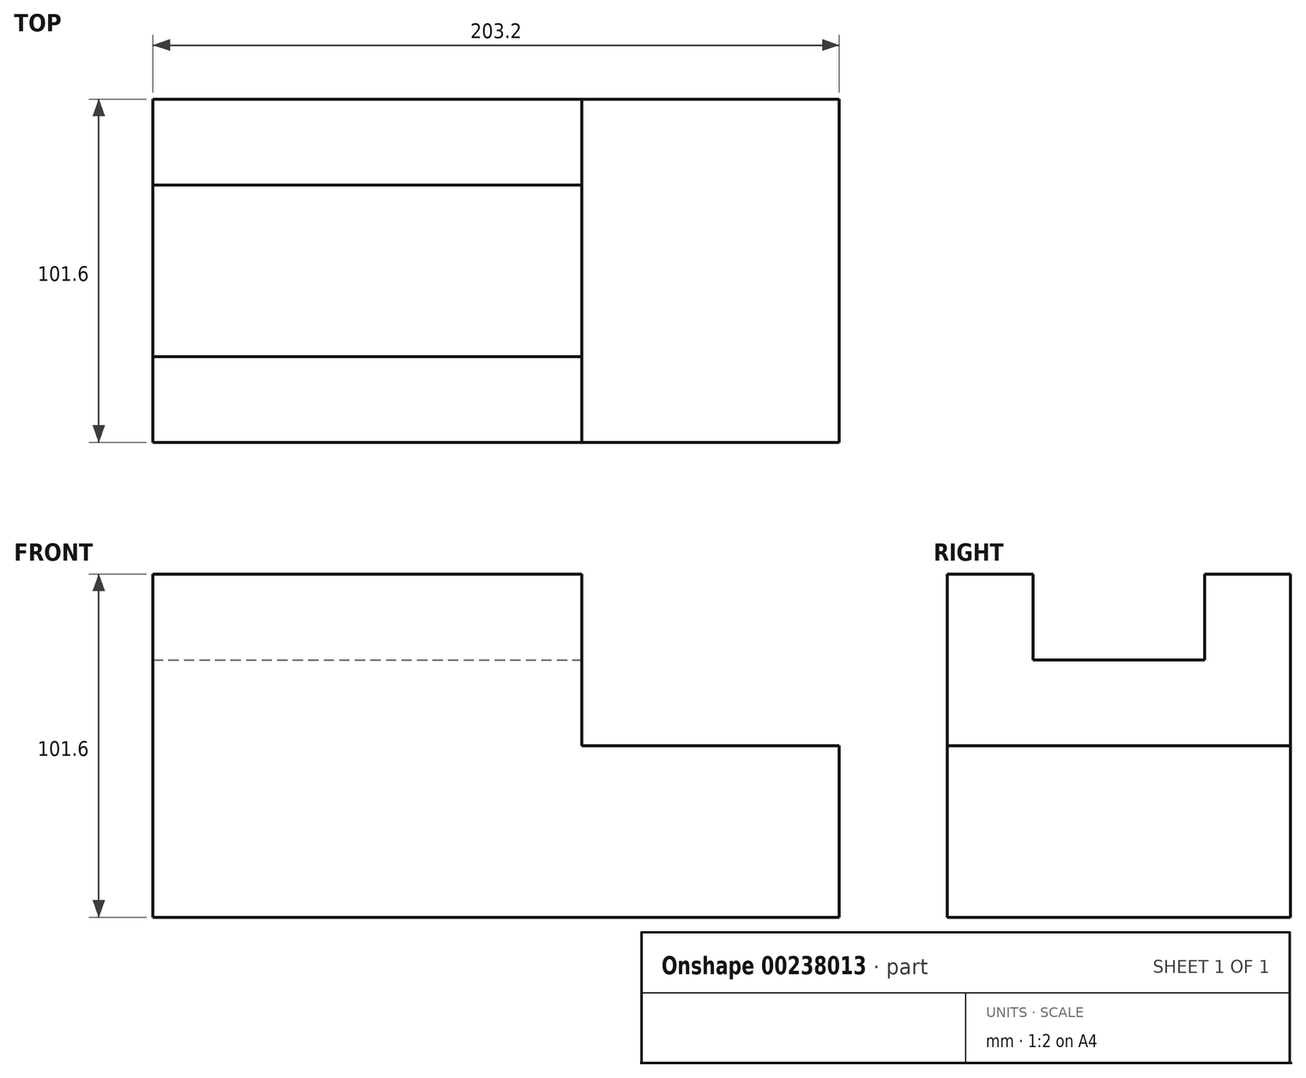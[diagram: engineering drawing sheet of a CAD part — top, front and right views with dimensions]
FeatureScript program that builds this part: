
annotation { "Feature Type Name" : "Feature", "Feature Type Description" : "" }
export const myFeature = defineFeature(function(context is Context, id is Id, definition is map)
    precondition{}
    {
        {
            var Q0;
            Q0=qCreatedBy(makeId("Front.planeOp"),FACE);
            var sketch = newSketch(context, id + "F0", { "sketchPlane" : qUnion([Q0])});
            skLineSegment(sketch, "E0.bottom", {"start": v(-132.5, 56.94) * mm, "end": v(70.7, 56.94) * mm});
            skLineSegment(sketch, "E0.top", {"start": v(-132.5, -44.66) * mm, "end": v(70.7, -44.66) * mm});
            skLineSegment(sketch, "E0.left", {"start": v(-132.5, 56.94) * mm, "end": v(-132.5, -44.66) * mm});
            skLineSegment(sketch, "E0.right", {"start": v(70.7, 56.94) * mm, "end": v(70.7, -44.66) * mm});
            skSolve(sketch);
        }
        {
            var Q0;
            Q0=makeQuery(id+"F0.imprint","IMPRINT",FACE,{"disambiguationData":[TD([[makeQuery(id+"F0.imprint","IMPRINT",EDGE,{"derivedFrom":sQuery(id+"F0.wireOp",EDGE,"E0.bottom")}),-1.0]])]});
            extrude(context, id + "F1", {"entities" : qUnion([Q0]), "depth" : 101.6 * mm});
        }
        {
            var Q0;
            Q0=makeQuery(id+"F1.opExtrude","CAP_FACE",FACE,{"disambiguationData":[OSD([sQuery(id+"F0.wireOp",EDGE,"E0.bottom"),sQuery(id+"F0.wireOp",EDGE,"E0.top"),sQuery(id+"F0.wireOp",EDGE,"E0.left"),sQuery(id+"F0.wireOp",EDGE,"E0.right")])],"isStart":false});
            var sketch = newSketch(context, id + "F2", { "sketchPlane" : qUnion([Q0])});
            skLineSegment(sketch, "E1.bottom", {"start": v(70.7, 56.94) * mm, "end": v(-5.5, 56.94) * mm});
            skLineSegment(sketch, "E1.top", {"start": v(70.7, 6.14) * mm, "end": v(-5.5, 6.14) * mm});
            skLineSegment(sketch, "E1.left", {"start": v(70.7, 56.94) * mm, "end": v(70.7, 6.14) * mm});
            skLineSegment(sketch, "E1.right", {"start": v(-5.5, 56.94) * mm, "end": v(-5.5, 6.14) * mm});
            skSolve(sketch);
        }
        {
            var Q0;
            Q0=makeQuery(id+"F2.imprint","IMPRINT",FACE,{"disambiguationData":[TD([[makeQuery(id+"F2.imprint","IMPRINT",EDGE,{"derivedFrom":sQuery(id+"F2.wireOp",EDGE,"E1.bottom")}),-1.0]])]});
            extrude(context, id + "F3", {"entities" : qUnion([Q0]), "operationType" : NewBodyOperationType.REMOVE, "oppositeDirection" : true, "depth" : 101.6 * mm});
        }
        {
            var Q0;
            Q0=makeQuery(id+"F1.opExtrude","SWEPT_FACE",FACE,{"disambiguationData":[OSD([sQuery(id+"F0.wireOp",EDGE,"E0.bottom")])]});
            var sketch = newSketch(context, id + "F4", { "sketchPlane" : qUnion([Q0])});
            skLineSegment(sketch, "E2.bottom", {"start": v(-132.5, -76.2) * mm, "end": v(-5.5, -76.2) * mm});
            skLineSegment(sketch, "E2.top", {"start": v(-132.5, -25.4) * mm, "end": v(-5.5, -25.4) * mm});
            skLineSegment(sketch, "E2.left", {"start": v(-132.5, -76.2) * mm, "end": v(-132.5, -25.4) * mm});
            skLineSegment(sketch, "E2.right", {"start": v(-5.5, -76.2) * mm, "end": v(-5.5, -25.4) * mm});
            skSolve(sketch);
        }
        {
            var Q0;
            Q0=makeQuery(id+"F4.imprint","IMPRINT",FACE,{"disambiguationData":[TD([[makeQuery(id+"F4.imprint","IMPRINT",EDGE,{"derivedFrom":sQuery(id+"F4.wireOp",EDGE,"E2.bottom")}),1.0]])]});
            extrude(context, id + "F5", {"entities" : qUnion([Q0]), "operationType" : NewBodyOperationType.REMOVE, "oppositeDirection" : true, "depth" : 25.4 * mm});
        }
    });
